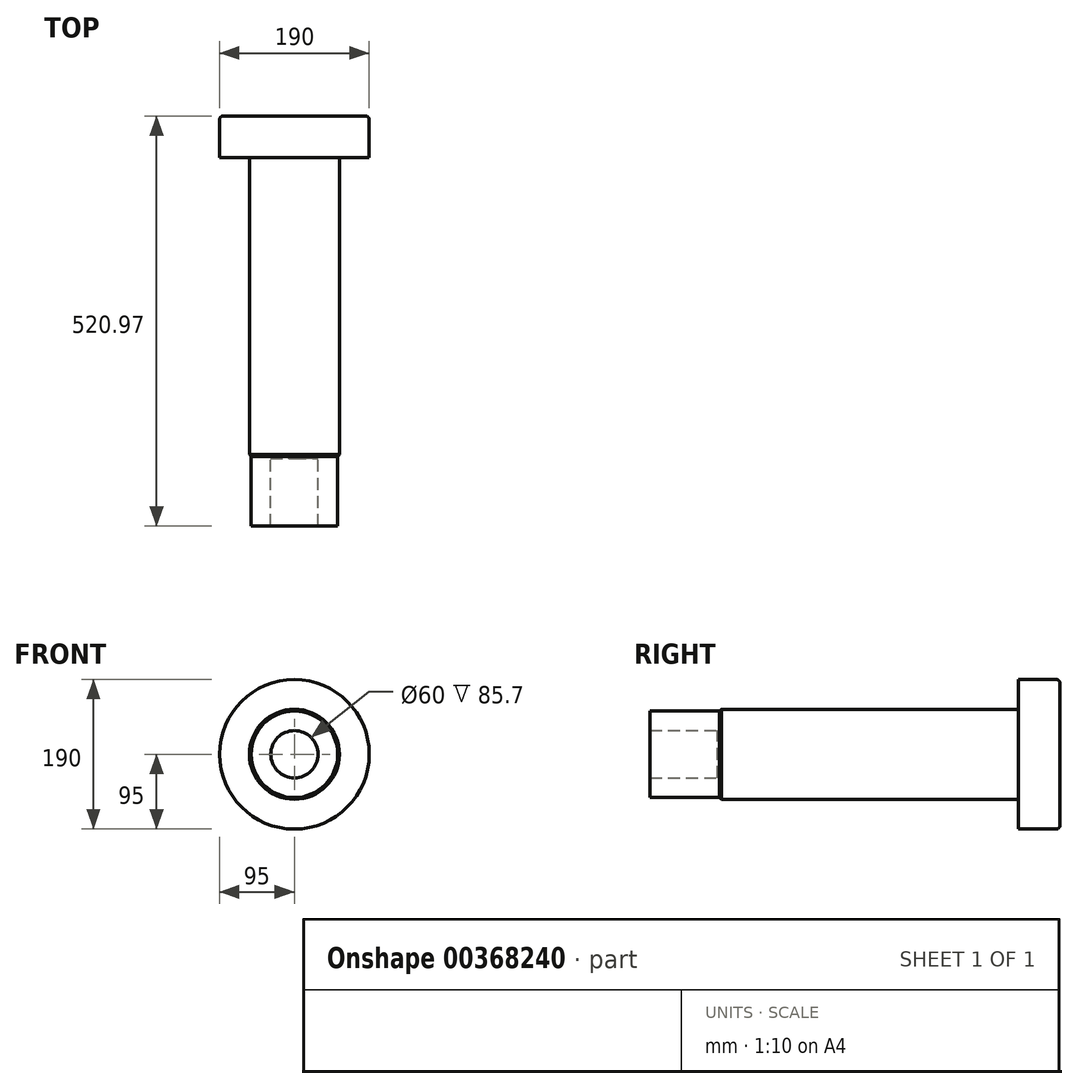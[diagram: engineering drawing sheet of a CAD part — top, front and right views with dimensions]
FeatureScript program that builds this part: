
annotation { "Feature Type Name" : "Feature", "Feature Type Description" : "" }
export const myFeature = defineFeature(function(context is Context, id is Id, definition is map)
    precondition{}
    {
        {
            var Q0;
            Q0=qCreatedBy(makeId("Front.planeOp"),FACE);
            var sketch = newSketch(context, id + "F0", { "sketchPlane" : qUnion([Q0])});
            skCircle(sketch, "E0", {"center": v(0, 0) * mm, "radius": 57.15 * mm});
            skSolve(sketch);
        }
        {
            var Q0;
            Q0=makeQuery(id+"F0.imprint","IMPRINT",FACE,{"disambiguationData":[TD([[makeQuery(id+"F0.imprint","IMPRINT",EDGE,{"derivedFrom":sQuery(id+"F0.wireOp",EDGE,"E0")}),1.0]])]});
            extrude(context, id + "F1", {"entities" : qUnion([Q0]), "depth" : 382.27 * mm});
        }
        {
            var Q0;
            Q0=qCreatedBy(makeId("Front.planeOp"),FACE);
            var sketch = newSketch(context, id + "F2", { "sketchPlane" : qUnion([Q0])});
            skCircle(sketch, "E1", {"center": v(0, 0) * mm, "radius": 95 * mm});
            skSolve(sketch);
        }
        {
            var Q0;
            Q0 = qSketchRegion(id + "F2", true);
            extrude(context, id + "F3", {"entities" : qUnion([Q0]), "operationType" : NewBodyOperationType.ADD, "oppositeDirection" : true, "depth" : 53 * mm});
        }
        {
            var Q0;
            Q0=makeQuery(id+"F3.opExtrude","CAP_EDGE",EDGE,{"disambiguationData":[OSD([sQuery(id+"F2.wireOp",EDGE,"E1")])],"isStart":false});
            fillet(context, id + "F4", {"entities" : qUnion([Q0]), "radius" : 5 * mm, "tangentPropagation" : true, "allowEdgeOverflow" : false});
        }
        {
            var Q0;
            Q0=makeQuery(id+"F1.opExtrude","CAP_FACE",FACE,{"disambiguationData":[OSD([sQuery(id+"F0.wireOp",EDGE,"E0")])],"isStart":false});
            var sketch = newSketch(context, id + "F5", { "sketchPlane" : qUnion([Q0])});
            skCircle(sketch, "E2", {"center": v(0, 0) * mm, "radius": 55 * mm});
            skCircle(sketch, "E3", {"center": v(0, 0) * mm, "radius": 30 * mm});
            skSolve(sketch);
        }
        {
            var Q0;
            Q0=makeQuery(id+"F5.imprint","IMPRINT",FACE,{"disambiguationData":[TD([[makeQuery(id+"F5.imprint","IMPRINT",EDGE,{"derivedFrom":sQuery(id+"F5.wireOp",EDGE,"E2")}),1.0]])]});
            extrude(context, id + "F6", {"entities" : qUnion([Q0]), "operationType" : NewBodyOperationType.ADD, "depth" : 85.7 * mm});
        }
        {
            var Q0;
            Q0=makeQuery(id+"F1.opExtrude","CAP_EDGE",EDGE,{"disambiguationData":[OSD([sQuery(id+"F0.wireOp",EDGE,"E0")])],"isStart":false});
            chamfer(context, id + "F7", {"entities" : qUnion([Q0]), "width" : 5 * mm, "tangentPropagation" : true});
        }
    });
